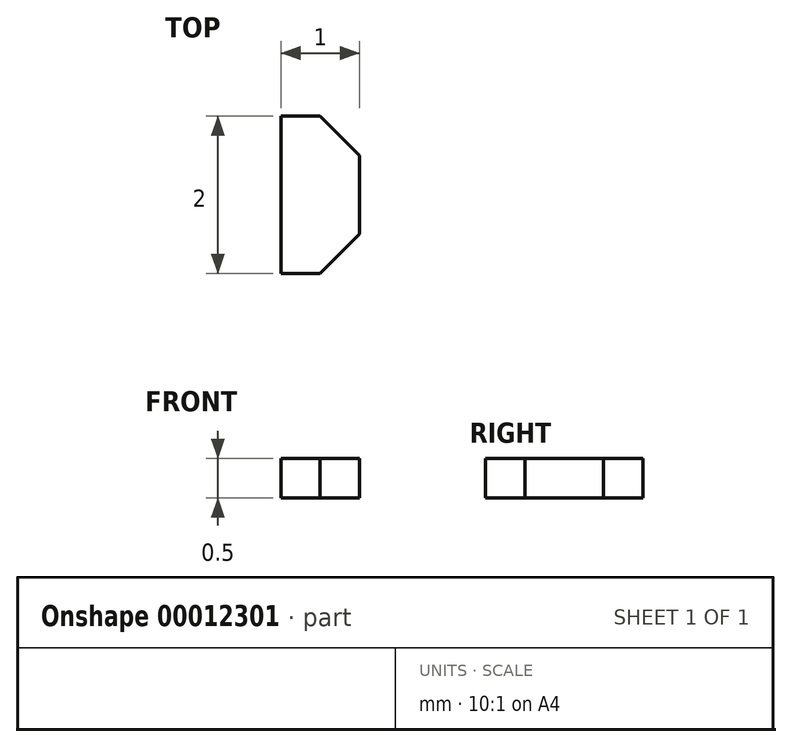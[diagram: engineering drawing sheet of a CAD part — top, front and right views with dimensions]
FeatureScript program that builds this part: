
annotation { "Feature Type Name" : "Feature", "Feature Type Description" : "" }
export const myFeature = defineFeature(function(context is Context, id is Id, definition is map)
    precondition{}
    {
        {
            var Q0;
            Q0=qCreatedBy(makeId("Top.planeOp"),FACE);
            var sketch = newSketch(context, id + "F0", { "sketchPlane" : qUnion([Q0])});
            skLineSegment(sketch, "E0.bottom", {"start": v(0.5, 2) * mm, "end": v(0, 2) * mm});
            skLineSegment(sketch, "E0.top", {"start": v(0.5, 0) * mm, "end": v(0, 0) * mm});
            skLineSegment(sketch, "E0.left", {"start": v(1, 1.5) * mm, "end": v(1, 0.5) * mm});
            skLineSegment(sketch, "E0.right", {"start": v(0, 2) * mm, "end": v(0, 0) * mm});
            skLineSegment(sketch, "E1", {"start": v(0, 1) * mm, "end": v(1.3, 1) * mm, "construction": true});
            skLineSegment(sketch, "E2", {"start": v(1, 2) * mm, "end": v(0, 1) * mm, "construction": true});
            skLineSegment(sketch, "E3", {"start": v(1, 0) * mm, "end": v(0, 1) * mm, "construction": true});
            skLineSegment(sketch, "E4", {"start": v(0.25, -0.36) * mm, "end": v(0.25, 2.4) * mm, "construction": true});
            skLineSegment(sketch, "E5", {"start": v(0.5, -0.31) * mm, "end": v(0.5, 2.3) * mm, "construction": true});
            skLineSegment(sketch, "E6", {"start": v(0.5, 2) * mm, "end": v(1, 1.5) * mm});
            skLineSegment(sketch, "E7", {"start": v(1, 0.5) * mm, "end": v(0.5, 0) * mm});
            skPoint(sketch, "E8.end.orphan", {"position": v(-0.58, 1.5) * mm});
            skPoint(sketch, "E9.orphan", {"position": v(-1.26, 0.5) * mm});
            skSolve(sketch);
        }
        {
            var Q0;
            Q0 = qSketchRegion(id + "F0", true);
            extrude(context, id + "F1", {"entities" : qUnion([Q0]), "depth" : 0.5 * mm});
        }
    });
